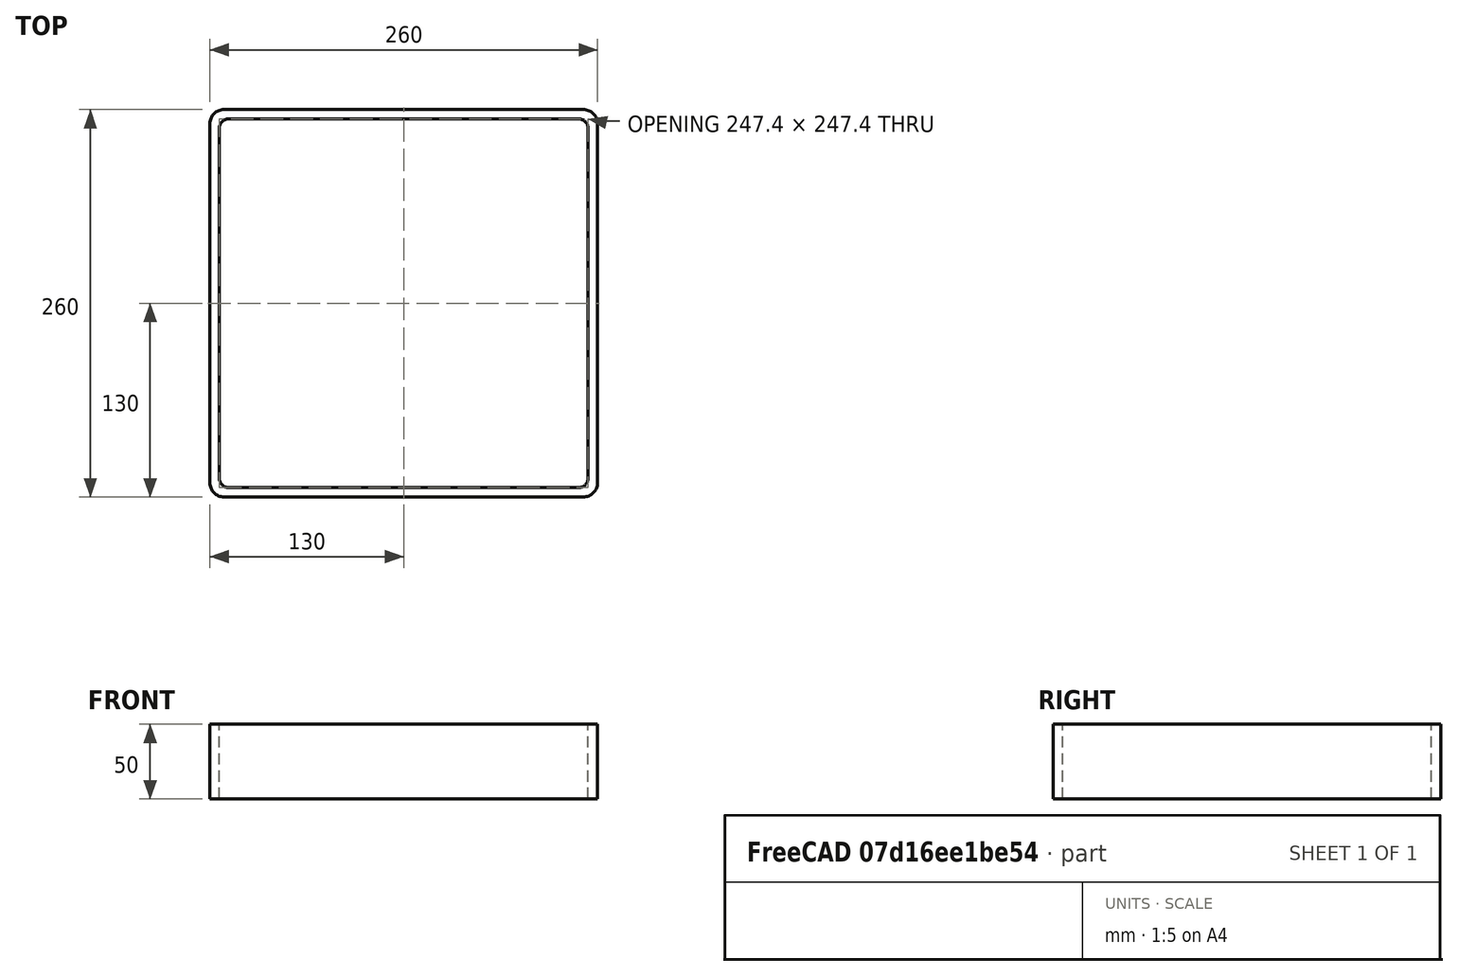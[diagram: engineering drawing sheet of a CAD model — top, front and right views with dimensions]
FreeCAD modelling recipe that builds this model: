
FCSTD DOCUMENT  (FreeCAD 0.15R4671 (Git))
Label: Square hollow section 260x260x6.3 EN10219 S235JRH
License: All rights reserved
LicenseURL: http://en.wikipedia.org/wiki/All_rights_reserved
objects: Sketcher::SketchObject×1, Part::Extrusion×1
note: 2 computed .brp shape members not serialized (recipe doc carries the construction recipe); baked Part::Feature solids carry a one-line shape summary decoded from their .brp

FEATURE [Sketcher::SketchObject] Sketch
  sketch-geometry (16):
    g0: LineSegment StartX=-117.4 StartY=123.7 StartZ=0 EndX=117.4 EndY=123.7 EndZ=0
    g1: LineSegment StartX=123.7 StartY=117.4 StartZ=0 EndX=123.7 EndY=-117.4 EndZ=0
    g2: LineSegment StartX=117.4 StartY=-123.7 StartZ=0 EndX=-117.4 EndY=-123.7 EndZ=0
    g3: LineSegment StartX=-123.7 StartY=-117.4 StartZ=0 EndX=-123.7 EndY=117.4 EndZ=0
    g4: LineSegment StartX=-120.55 StartY=130 StartZ=0 EndX=120.55 EndY=130 EndZ=0
    g5: LineSegment StartX=130 StartY=120.55 StartZ=0 EndX=130 EndY=-120.55 EndZ=0
    g6: LineSegment StartX=120.55 StartY=-130 StartZ=0 EndX=-120.55 EndY=-130 EndZ=0
    g7: LineSegment StartX=-130 StartY=-120.55 StartZ=0 EndX=-130 EndY=120.55 EndZ=0
    g8: ArcOfCircle CenterX=-117.4 CenterY=117.4 CenterZ=0 NormalX=0 NormalY=0 NormalZ=1 Radius=6.3 StartAngle=1.5708 EndAngle=3.14159
    g9: ArcOfCircle CenterX=117.4 CenterY=117.4 CenterZ=0 NormalX=0 NormalY=0 NormalZ=1 Radius=6.3 StartAngle=0 EndAngle=1.5708
    g10: ArcOfCircle CenterX=117.4 CenterY=-117.4 CenterZ=0 NormalX=0 NormalY=0 NormalZ=1 Radius=6.3 StartAngle=4.71239 EndAngle=6.28319
    g11: ArcOfCircle CenterX=-117.4 CenterY=-117.4 CenterZ=0 NormalX=0 NormalY=0 NormalZ=1 Radius=6.3 StartAngle=3.14159 EndAngle=4.71239
    g12: ArcOfCircle CenterX=120.55 CenterY=120.55 CenterZ=0 NormalX=0 NormalY=0 NormalZ=1 Radius=9.45 StartAngle=0 EndAngle=1.5708
    g13: ArcOfCircle CenterX=120.55 CenterY=-120.55 CenterZ=0 NormalX=0 NormalY=0 NormalZ=1 Radius=9.45 StartAngle=4.71239 EndAngle=6.28319
    g14: ArcOfCircle CenterX=-120.55 CenterY=-120.55 CenterZ=0 NormalX=0 NormalY=0 NormalZ=1 Radius=9.45 StartAngle=3.14159 EndAngle=4.71239
    g15: ArcOfCircle CenterX=-120.55 CenterY=120.55 CenterZ=0 NormalX=0 NormalY=0 NormalZ=1 Radius=9.45 StartAngle=1.5708 EndAngle=3.14159
  constraints (36):
    c: Horizontal(g2)
    c: Vertical(g3)
    c: Horizontal(g6)
    c: Vertical(g7)
    c: Tangent(g3,g8) = 1.5708
    c: Tangent(g0,g8) = 1.5708
    c: Tangent(g0,g9) = 1.5708
    c: Tangent(g1,g9) = 1.5708
    c: Tangent(g1,g10) = 1.5708
    c: Tangent(g2,g10) = 1.5708
    c: Tangent(g2,g11) = 1.5708
    c: Tangent(g3,g11) = 1.5708
    c: Tangent(g4,g12) = 1.5708
    c: Tangent(g5,g12) = 1.5708
    c: Tangent(g5,g13) = 1.5708
    c: Tangent(g6,g13) = 1.5708
    c: Tangent(g6,g14) = 1.5708
    c: Tangent(g7,g14) = 1.5708
    c: Tangent(g7,g15) = 1.5708
    c: Tangent(g4,g15) = 1.5708
    c: Equal(g9,g8)
    c: Equal(g9,g11)
    c: Equal(g9,g10)
    c: Equal(g12,g15)
    c: Equal(g12,g14)
    c: Equal(g12,g13)
    c: Symmetric(g4,g6,g-1)
    c: Symmetric(g7,g5,g-2)
    c: DistanceY(g4,g6) = -260
    c: DistanceX(g7,g5) = 260
    c: Symmetric(g3,g1,g-2)
    c: Symmetric(g0,g2,g-1)
    c: DistanceY(g0,g4) = 6.3
    c: DistanceX(g5,g1) = -6.3
    c: Radius(g9) = 6.3
    c: Radius(g12) = 9.45
FEATURE [Part::Extrusion] Extrude  label="Square hollow section 260x260x6.3 EN10219 S235JRH"
  Base = -> Sketch
  Dir = (0,0,50)
  Solid = true
